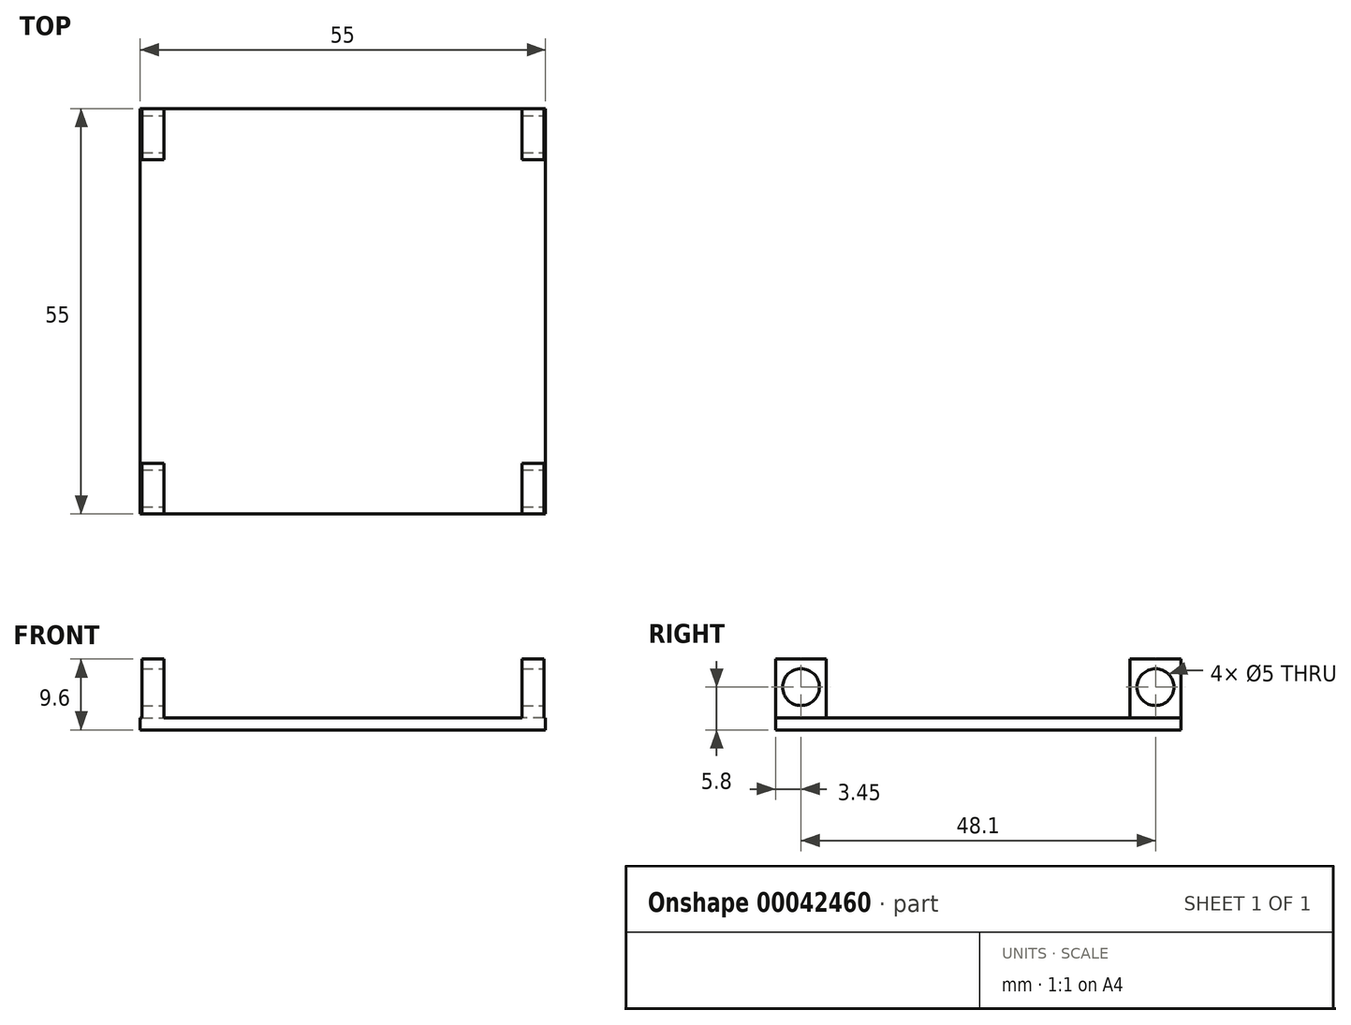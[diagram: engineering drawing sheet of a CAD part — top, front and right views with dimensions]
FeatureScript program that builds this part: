
annotation { "Feature Type Name" : "Feature", "Feature Type Description" : "" }
export const myFeature = defineFeature(function(context is Context, id is Id, definition is map)
    precondition{}
    {
        {
            var Q0;
            Q0=qCreatedBy(makeId("Top.planeOp"),FACE);
            var sketch = newSketch(context, id + "F0", { "sketchPlane" : qUnion([Q0])});
            skLineSegment(sketch, "E0.rect.bottom", {"start": v(27.5, 27.5) * mm, "end": v(-27.5, 27.5) * mm});
            skLineSegment(sketch, "E0.rect.top", {"start": v(27.5, -27.5) * mm, "end": v(-27.5, -27.5) * mm});
            skLineSegment(sketch, "E0.rect.left", {"start": v(27.5, 27.5) * mm, "end": v(27.5, -27.5) * mm});
            skLineSegment(sketch, "E0.rect.right", {"start": v(-27.5, 27.5) * mm, "end": v(-27.5, -27.5) * mm});
            skPoint(sketch, "E0.rect.middle", {"position": v(0, 0) * mm});
            skSolve(sketch);
        }
        {
            var Q0;
            Q0 = qSketchRegion(id + "F0", true);
            extrude(context, id + "F1", {"entities" : qUnion([Q0]), "depth" : 1.6 * mm});
        }
        {
            var Q0;
            Q0=makeQuery(id+"F1.opExtrude","CAP_FACE",FACE,{"disambiguationData":[OSD([sQuery(id+"F0.wireOp",EDGE,"E0.rect.bottom"),sQuery(id+"F0.wireOp",EDGE,"E0.rect.top"),sQuery(id+"F0.wireOp",EDGE,"E0.rect.left"),sQuery(id+"F0.wireOp",EDGE,"E0.rect.right")])],"isStart":false});
            var sketch = newSketch(context, id + "F2", { "sketchPlane" : qUnion([Q0])});
            skLineSegment(sketch, "E1.bottom", {"start": v(27.3, 27.5) * mm, "end": v(24.3, 27.5) * mm});
            skLineSegment(sketch, "E1.top", {"start": v(27.3, 20.6) * mm, "end": v(24.3, 20.6) * mm});
            skLineSegment(sketch, "E1.left", {"start": v(27.3, 27.5) * mm, "end": v(27.3, 20.6) * mm});
            skLineSegment(sketch, "E1.right", {"start": v(24.3, 27.5) * mm, "end": v(24.3, 20.6) * mm});
            skLineSegment(sketch, "E2.bottom", {"start": v(27.3, -27.5) * mm, "end": v(24.3, -27.5) * mm});
            skLineSegment(sketch, "E2.top", {"start": v(27.3, -20.6) * mm, "end": v(24.3, -20.6) * mm});
            skLineSegment(sketch, "E2.left", {"start": v(27.3, -27.5) * mm, "end": v(27.3, -20.6) * mm});
            skLineSegment(sketch, "E2.right", {"start": v(24.3, -27.5) * mm, "end": v(24.3, -20.6) * mm});
            skLineSegment(sketch, "E3", {"start": v(0, 0) * mm, "end": v(0, 39.26) * mm, "construction": true});
            skLineSegment(sketch, "E4.MirrorCS", {"start": v(-27.3, -27.5) * mm, "end": v(-27.3, -20.6) * mm});
            skLineSegment(sketch, "E5.MirrorCS", {"start": v(-27.3, -20.6) * mm, "end": v(-24.3, -20.6) * mm});
            skLineSegment(sketch, "E6.MirrorCS", {"start": v(-27.3, -27.5) * mm, "end": v(-24.3, -27.5) * mm});
            skLineSegment(sketch, "E7.MirrorCS", {"start": v(-24.3, 27.5) * mm, "end": v(-24.3, 20.6) * mm});
            skLineSegment(sketch, "E8.MirrorCS", {"start": v(-27.3, 27.5) * mm, "end": v(-27.3, 20.6) * mm});
            skLineSegment(sketch, "E9.MirrorCS", {"start": v(-27.3, 20.6) * mm, "end": v(-24.3, 20.6) * mm});
            skLineSegment(sketch, "E10.MirrorCS", {"start": v(-27.3, 27.5) * mm, "end": v(-24.3, 27.5) * mm});
            skLineSegment(sketch, "E11.MirrorCS", {"start": v(-24.3, -27.5) * mm, "end": v(-24.3, -20.6) * mm});
            skSolve(sketch);
        }
        {
            var Q0;
            Q0 = qSketchRegion(id + "F2", true);
            extrude(context, id + "F3", {"entities" : qUnion([Q0]), "operationType" : NewBodyOperationType.ADD, "depth" : 8 * mm});
        }
        {
            var Q0;
            Q0=makeQuery(id+"F3.opExtrude","SWEPT_FACE",FACE,{"disambiguationData":[OSD([sQuery(id+"F2.wireOp",EDGE,"E1.left")])]});
            var sketch = newSketch(context, id + "F4", { "sketchPlane" : qUnion([Q0])});
            skCircle(sketch, "E12", {"center": v(24.05, 5.8) * mm, "radius": 2.5 * mm});
            skCircle(sketch, "E13", {"center": v(-24.05, 5.8) * mm, "radius": 2.5 * mm});
            skLineSegment(sketch, "E14", {"start": v(24.05, 9.6) * mm, "end": v(24.05, 1.6) * mm, "construction": true});
            skLineSegment(sketch, "E15", {"start": v(-24.05, 9.6) * mm, "end": v(-24.05, 1.6) * mm, "construction": true});
            skSolve(sketch);
        }
        {
            var Q0;
            Q0 = qSketchRegion(id + "F4", true);
            extrude(context, id + "F5", {"entities" : qUnion([Q0]), "operationType" : NewBodyOperationType.REMOVE, "endBound" : BoundingType.THROUGH_ALL, "oppositeDirection" : true, "depth" : 25.4 * mm});
        }
    });
